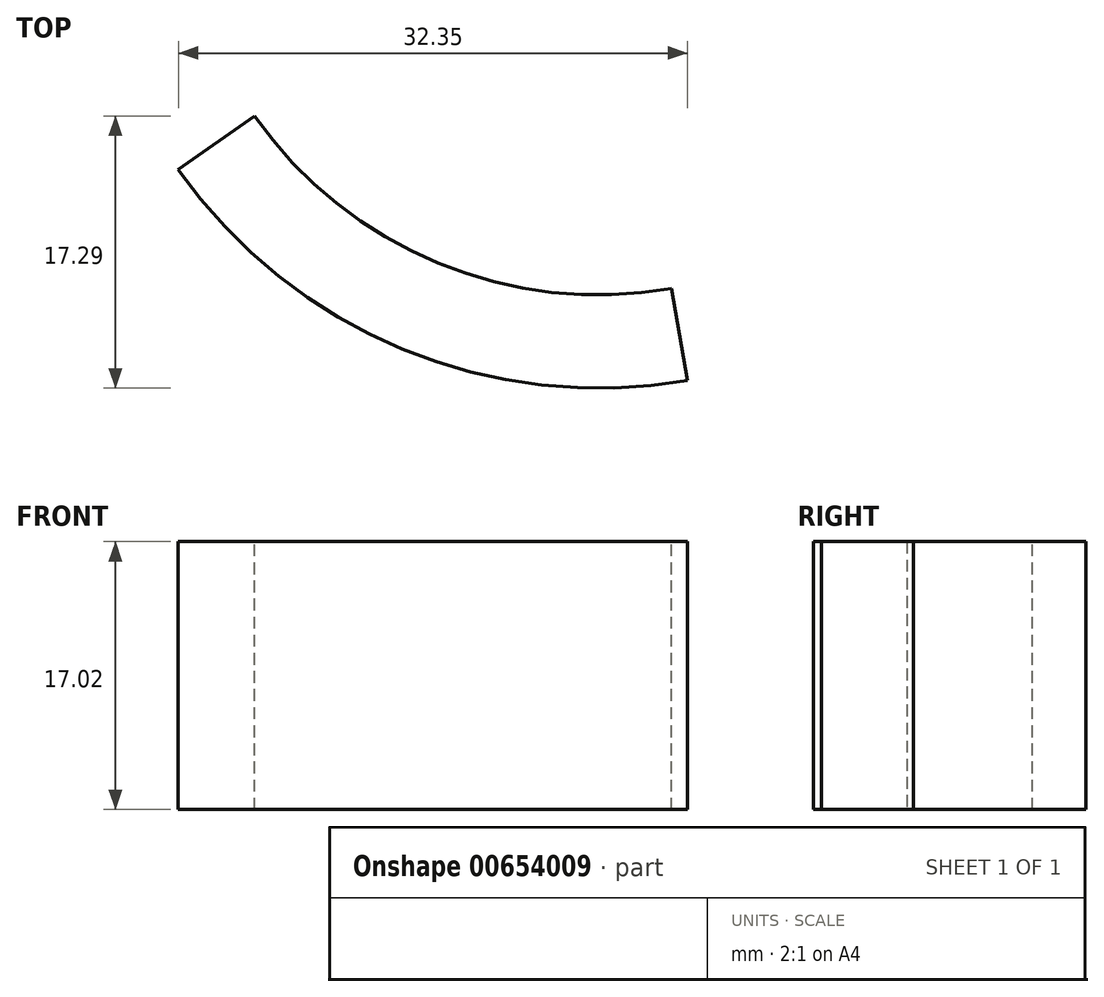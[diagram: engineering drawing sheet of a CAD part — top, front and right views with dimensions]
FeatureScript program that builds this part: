
annotation { "Feature Type Name" : "Feature", "Feature Type Description" : "" }
export const myFeature = defineFeature(function(context is Context, id is Id, definition is map)
    precondition{}
    {
        {
            var Q0;
            Q0=qCreatedBy(makeId("Right.planeOp"),FACE);
            var sketch = newSketch(context, id + "F0", { "sketchPlane" : qUnion([Q0])});
            skLineSegment(sketch, "E0.bottom", {"start": v(-26.67, 0) * mm, "end": v(-32.59, 0) * mm});
            skLineSegment(sketch, "E0.top", {"start": v(-26.67, 17.02) * mm, "end": v(-32.59, 17.02) * mm});
            skLineSegment(sketch, "E0.left", {"start": v(-26.67, 0) * mm, "end": v(-26.67, 17.02) * mm});
            skLineSegment(sketch, "E0.right", {"start": v(-32.59, 0) * mm, "end": v(-32.59, 17.02) * mm});
            skSolve(sketch);
        }
        {
            var Q0;
            Q0=qCreatedBy(makeId("Right.planeOp"),FACE);
            var sketch = newSketch(context, id + "F1", { "sketchPlane" : qUnion([Q0])});
            skLineSegment(sketch, "E1", {"start": v(0, 0) * mm, "end": v(0, 54.44) * mm});
            skSolve(sketch);
        }
        {
            var Q0;
            Q0 = qSketchRegion(id + "F0", true);
            var Q1;
            Q1=sQuery(id+"F1.wireOp",EDGE,"E1");
            revolve(context, id + "F2", {"entities" : qUnion([Q0]), "axis" : qUnion([Q1]), "revolveType" : RevolveType.TWO_DIRECTIONS, "angle" : 10 * degree, "angleBack" : 305 * degree});
        }
    });
